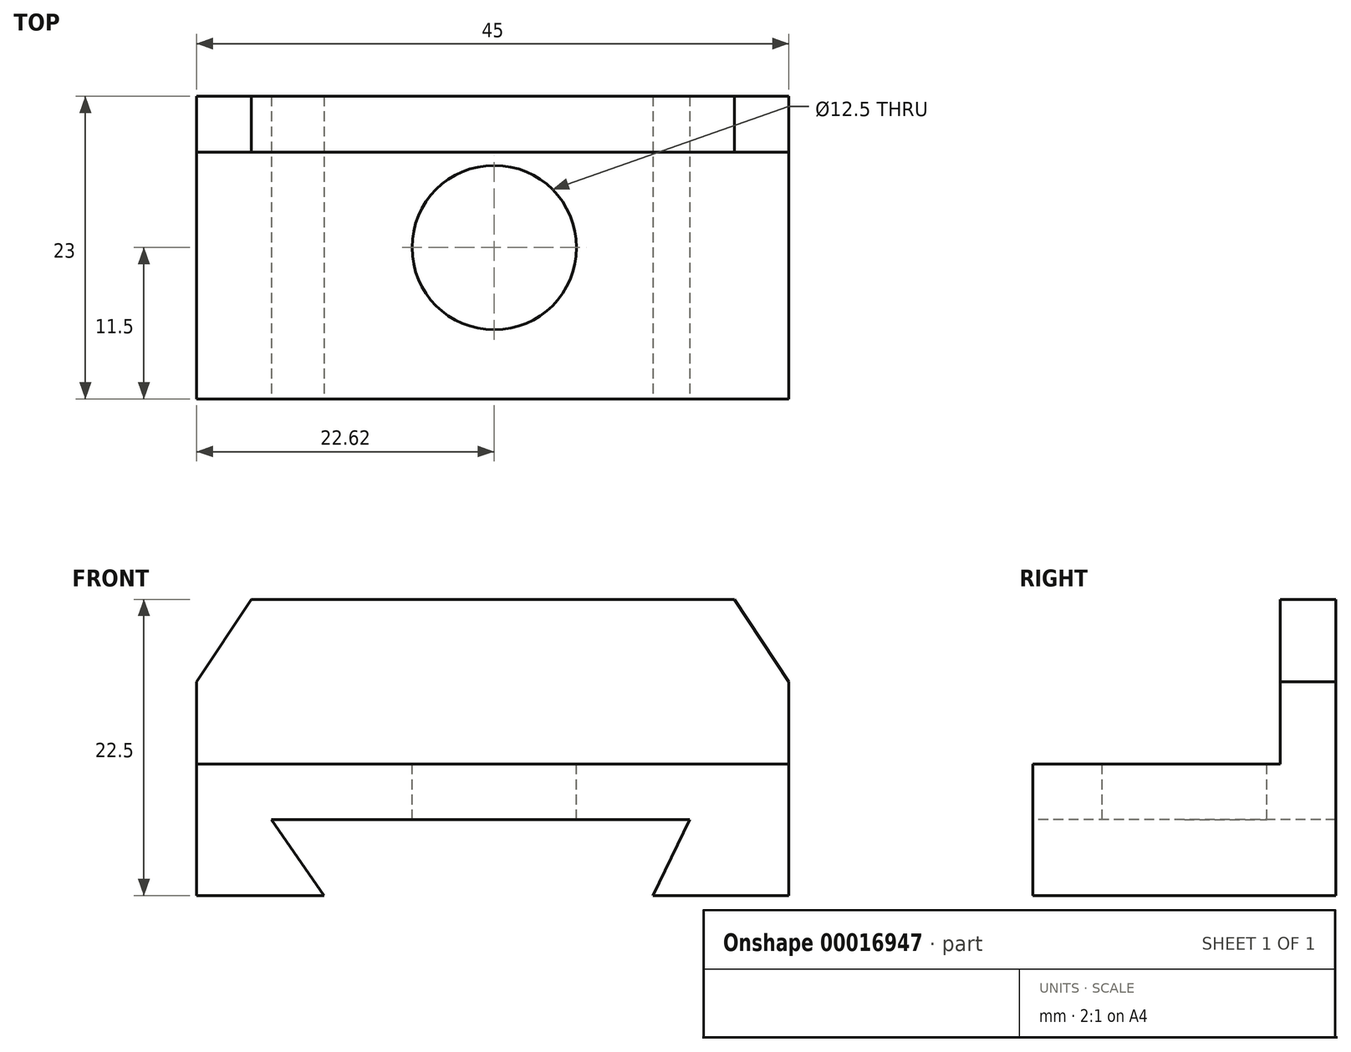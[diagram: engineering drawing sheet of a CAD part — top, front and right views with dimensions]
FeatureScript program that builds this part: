
annotation { "Feature Type Name" : "Feature", "Feature Type Description" : "" }
export const myFeature = defineFeature(function(context is Context, id is Id, definition is map)
    precondition{}
    {
        {
            var Q0;
            Q0=qCreatedBy(makeId("Top.planeOp"),FACE);
            var sketch = newSketch(context, id + "F0", { "sketchPlane" : qUnion([Q0])});
            skLineSegment(sketch, "E0.bottom", {"start": v(-22.62, 9.53) * mm, "end": v(22.38, 9.53) * mm});
            skLineSegment(sketch, "E0.top", {"start": v(-22.62, -13.47) * mm, "end": v(22.38, -13.47) * mm});
            skLineSegment(sketch, "E0.left", {"start": v(-22.62, 9.53) * mm, "end": v(-22.62, -13.47) * mm});
            skLineSegment(sketch, "E0.right", {"start": v(22.38, 9.53) * mm, "end": v(22.38, -13.47) * mm});
            skSolve(sketch);
        }
        {
            var Q0;
            Q0=makeQuery(id+"F0.imprint","IMPRINT",FACE,{"disambiguationData":[TD([[makeQuery(id+"F0.imprint","IMPRINT",EDGE,{"derivedFrom":sQuery(id+"F0.wireOp",EDGE,"E0.bottom")}),-1.0]])]});
            extrude(context, id + "F1", {"entities" : qUnion([Q0]), "depth" : 10 * mm});
        }
        {
            var Q0;
            Q0=makeQuery(id+"F1.opExtrude","SWEPT_FACE",FACE,{"disambiguationData":[OSD([sQuery(id+"F0.wireOp",EDGE,"E0.top")])]});
            var sketch = newSketch(context, id + "F2", { "sketchPlane" : qUnion([Q0])});
            skLineSegment(sketch, "E1", {"start": v(-12.95, 0) * mm, "end": v(-16.95, 5.77) * mm});
            skLineSegment(sketch, "E2", {"start": v(-16.95, 5.77) * mm, "end": v(14.83, 5.77) * mm});
            skLineSegment(sketch, "E3", {"start": v(14.83, 5.77) * mm, "end": v(12.05, 0) * mm});
            skLineSegment(sketch, "E4", {"start": v(12.05, 0) * mm, "end": v(-12.95, 0) * mm});
            skSolve(sketch);
        }
        {
            var Q0;
            Q0=makeQuery(id+"F2.imprint","IMPRINT",FACE,{"disambiguationData":[TD([[makeQuery(id+"F2.imprint","IMPRINT",EDGE,{"derivedFrom":sQuery(id+"F2.wireOp",EDGE,"E1")}),-1.0]])]});
            extrude(context, id + "F3", {"entities" : qUnion([Q0]), "operationType" : NewBodyOperationType.REMOVE, "endBound" : BoundingType.THROUGH_ALL, "oppositeDirection" : true, "depth" : 25 * mm});
        }
        {
            var Q0;
            Q0=makeQuery(id+"F1.opExtrude","CAP_FACE",FACE,{"disambiguationData":[OSD([sQuery(id+"F0.wireOp",EDGE,"E0.bottom"),sQuery(id+"F0.wireOp",EDGE,"E0.top"),sQuery(id+"F0.wireOp",EDGE,"E0.left"),sQuery(id+"F0.wireOp",EDGE,"E0.right")])],"isStart":false});
            var sketch = newSketch(context, id + "F4", { "sketchPlane" : qUnion([Q0])});
            skCircle(sketch, "E5", {"center": v(0, -1.97) * mm, "radius": 6.25 * mm});
            skSolve(sketch);
        }
        {
            var Q0;
            Q0=makeQuery(id+"F4.imprint","IMPRINT",FACE,{"disambiguationData":[TD([[makeQuery(id+"F4.imprint","IMPRINT",EDGE,{"derivedFrom":sQuery(id+"F4.wireOp",EDGE,"E5")}),1.0]])]});
            extrude(context, id + "F5", {"entities" : qUnion([Q0]), "operationType" : NewBodyOperationType.REMOVE, "endBound" : BoundingType.THROUGH_ALL, "oppositeDirection" : true, "depth" : 25 * mm});
        }
        {
            var Q0;
            Q0=makeQuery(id+"F1.opExtrude","CAP_FACE",FACE,{"disambiguationData":[OSD([sQuery(id+"F0.wireOp",EDGE,"E0.bottom"),sQuery(id+"F0.wireOp",EDGE,"E0.top"),sQuery(id+"F0.wireOp",EDGE,"E0.left"),sQuery(id+"F0.wireOp",EDGE,"E0.right")])],"isStart":false});
            var sketch = newSketch(context, id + "F6", { "sketchPlane" : qUnion([Q0])});
            skLineSegment(sketch, "E6", {"start": v(-22.62, 5.3) * mm, "end": v(22.38, 5.3) * mm});
            skSolve(sketch);
        }
        {
            var Q0;
            {var subQ1=sQuery(id+"F6.wireOp",EDGE,"E6");Q0=makeQuery(id+"F6.imprint","IMPRINT",FACE,{"disambiguationData":[TD([[makeQuery(id+"F6.imprint","IMPRINT",EDGE,{"derivedFrom":subQ1}),1.0]])]});}
            extrude(context, id + "F7", {"entities" : qUnion([Q0]), "operationType" : NewBodyOperationType.ADD, "depth" : 12.5 * mm});
        }
        {
            var Q0;
            Q0=makeQuery(id+"F7.opExtrude","SWEPT_FACE",FACE,{"disambiguationData":[OSD([sQuery(id+"F6.wireOp",EDGE,"E6")])]});
            var sketch = newSketch(context, id + "F8", { "sketchPlane" : qUnion([Q0])});
            skLineSegment(sketch, "E7", {"start": v(18.24, 22.5) * mm, "end": v(22.38, 16.25) * mm});
            skLineSegment(sketch, "E8", {"start": v(22.38, 16.25) * mm, "end": v(22.38, 22.5) * mm});
            skLineSegment(sketch, "E9", {"start": v(22.38, 22.5) * mm, "end": v(18.24, 22.5) * mm});
            skLineSegment(sketch, "E10", {"start": v(-18.47, 22.5) * mm, "end": v(-22.62, 16.25) * mm});
            skLineSegment(sketch, "E11", {"start": v(-22.62, 16.25) * mm, "end": v(-22.62, 22.5) * mm});
            skLineSegment(sketch, "E12", {"start": v(-22.62, 22.5) * mm, "end": v(-18.47, 22.5) * mm});
            skSolve(sketch);
        }
        {
            var Q0;
            Q0=makeQuery(id+"F8.imprint","IMPRINT",FACE,{"disambiguationData":[TD([[makeQuery(id+"F8.imprint","IMPRINT",EDGE,{"derivedFrom":sQuery(id+"F8.wireOp",EDGE,"E10")}),-1.0]])]});
            var Q1;
            Q1=makeQuery(id+"F8.imprint","IMPRINT",FACE,{"disambiguationData":[TD([[makeQuery(id+"F8.imprint","IMPRINT",EDGE,{"derivedFrom":sQuery(id+"F8.wireOp",EDGE,"E7")}),1.0]])]});
            extrude(context, id + "F9", {"entities" : qUnion([Q0, Q1]), "operationType" : NewBodyOperationType.REMOVE, "endBound" : BoundingType.THROUGH_ALL, "oppositeDirection" : true, "depth" : 25 * mm});
        }
    });
